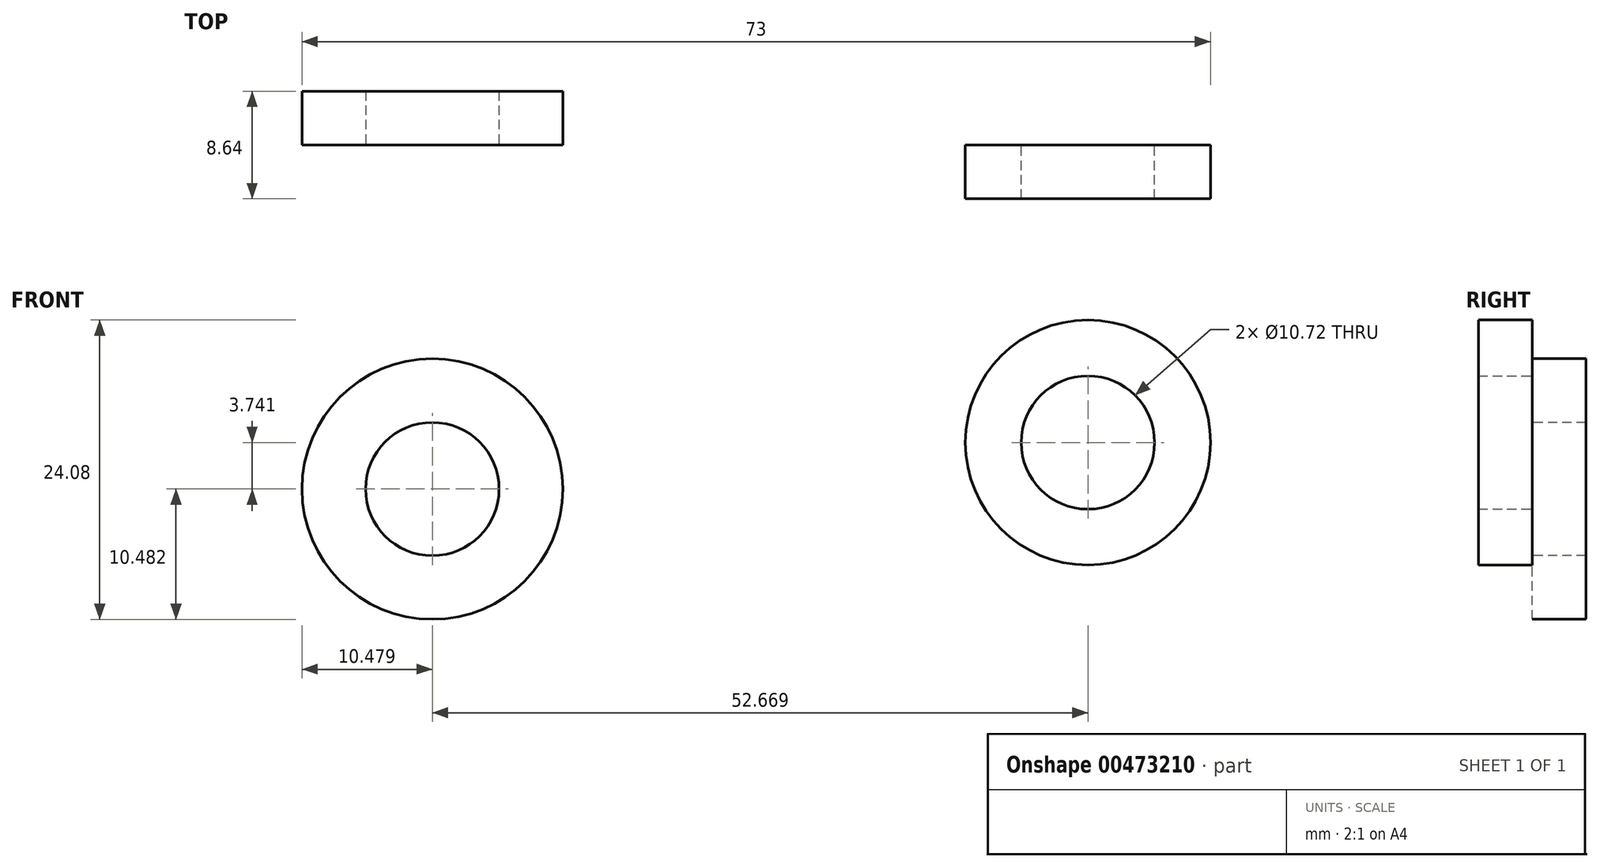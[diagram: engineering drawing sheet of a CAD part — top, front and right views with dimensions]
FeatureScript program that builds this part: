
annotation { "Feature Type Name" : "Feature", "Feature Type Description" : "" }
export const myFeature = defineFeature(function(context is Context, id is Id, definition is map)
    precondition{}
    {
        {
            var Q0;
            Q0=qCreatedBy(makeId("Front.planeOp"),FACE);
            var sketch = newSketch(context, id + "F0", { "sketchPlane" : qUnion([Q0])});
            skCircle(sketch, "E0", {"center": v(-24.75, 23.31) * mm, "radius": 10.48 * mm});
            skCircle(sketch, "E1", {"center": v(-24.75, 23.31) * mm, "radius": 5.36 * mm});
            skSolve(sketch);
        }
        {
            var Q0;
            Q0 = qSketchRegion(id + "F0", true);
            extrude(context, id + "F1", {"entities" : qUnion([Q0]), "oppositeDirection" : true, "depth" : 4.32 * mm});
        }
        {
            var Q0;
            Q0=qCreatedBy(makeId("Front.planeOp"),FACE);
            var sketch = newSketch(context, id + "F2", { "sketchPlane" : qUnion([Q0])});
            skCircle(sketch, "E2", {"center": v(27.92, 27.05) * mm, "radius": 9.85 * mm});
            skCircle(sketch, "E3", {"center": v(27.92, 27.05) * mm, "radius": 5.36 * mm});
            skSolve(sketch);
        }
        {
            var Q0;
            Q0 = qSketchRegion(id + "F2", true);
            extrude(context, id + "F3", {"entities" : qUnion([Q0]), "depth" : 4.32 * mm});
        }
    });
